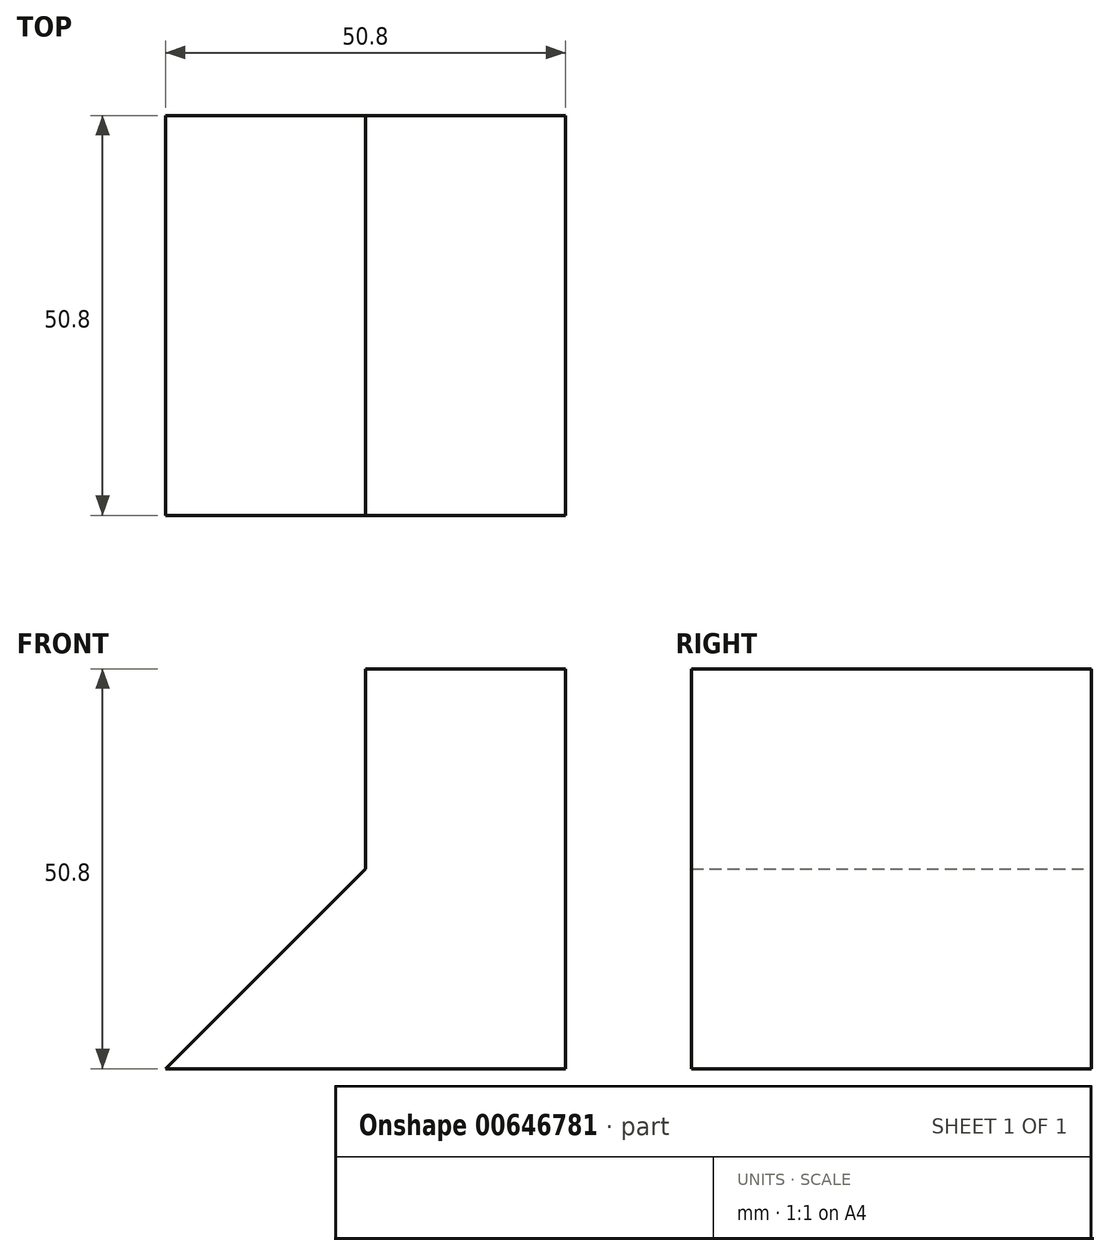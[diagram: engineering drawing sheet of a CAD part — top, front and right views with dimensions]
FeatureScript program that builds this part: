
annotation { "Feature Type Name" : "Feature", "Feature Type Description" : "" }
export const myFeature = defineFeature(function(context is Context, id is Id, definition is map)
    precondition{}
    {
        {
            var Q0;
            Q0=qCreatedBy(makeId("Front.planeOp"),FACE);
            var sketch = newSketch(context, id + "F0", { "sketchPlane" : qUnion([Q0])});
            skLineSegment(sketch, "E0", {"start": v(-33.9, 0) * mm, "end": v(16.9, 0) * mm});
            skLineSegment(sketch, "E1", {"start": v(16.9, 0) * mm, "end": v(16.9, 50.8) * mm});
            skLineSegment(sketch, "E2", {"start": v(16.9, 50.8) * mm, "end": v(-8.5, 50.8) * mm});
            skLineSegment(sketch, "E3", {"start": v(-8.5, 50.8) * mm, "end": v(-8.5, 25.4) * mm});
            skLineSegment(sketch, "E4", {"start": v(-8.5, 25.4) * mm, "end": v(-33.9, 0) * mm});
            skSolve(sketch);
        }
        {
            var Q0;
            Q0 = qSketchRegion(id + "F0", true);
            extrude(context, id + "F1", {"entities" : qUnion([Q0]), "depth" : 50.8 * mm, "offsetDistance" : 25.4 * mm});
        }
    });
